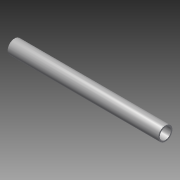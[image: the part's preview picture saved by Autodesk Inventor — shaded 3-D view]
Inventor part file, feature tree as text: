
AUTODESK INVENTOR PART (.ipt)
format: ipt  version: 2014 (Build 180170000, 170)  size: 101,376 bytes
history: native  units: in
note: dims shown in document units (in); Inventor stores cm internally (conversion verified against a paired STEP export)
features: other x2, extrude x1, imported_body x1, sketch x1
ambient origin geometry x8: Origin, YZ Plane, XZ Plane, XY Plane, X Axis, Y Axis, Z Axis, Center Point
bodies: Body1 (feature_tree)
feature tree (5):
  parser-record x1  (decoder bookkeeping rows leaked as tree rows — omitted from the tree; the rows remain in map.json)
  other  "4347K3111"
  extrude  "Extrusion2"  [1 undecoded]
  imported_body  "Base1"
  sketch  "Sketch2"  dims[d2=3.0in d3=0.0in]
note: 1 required parameter value undecoded (feature->parameter linkage not recoverable at this tier; creation-order binding heuristic only, values carry confidence <= 0.55)
